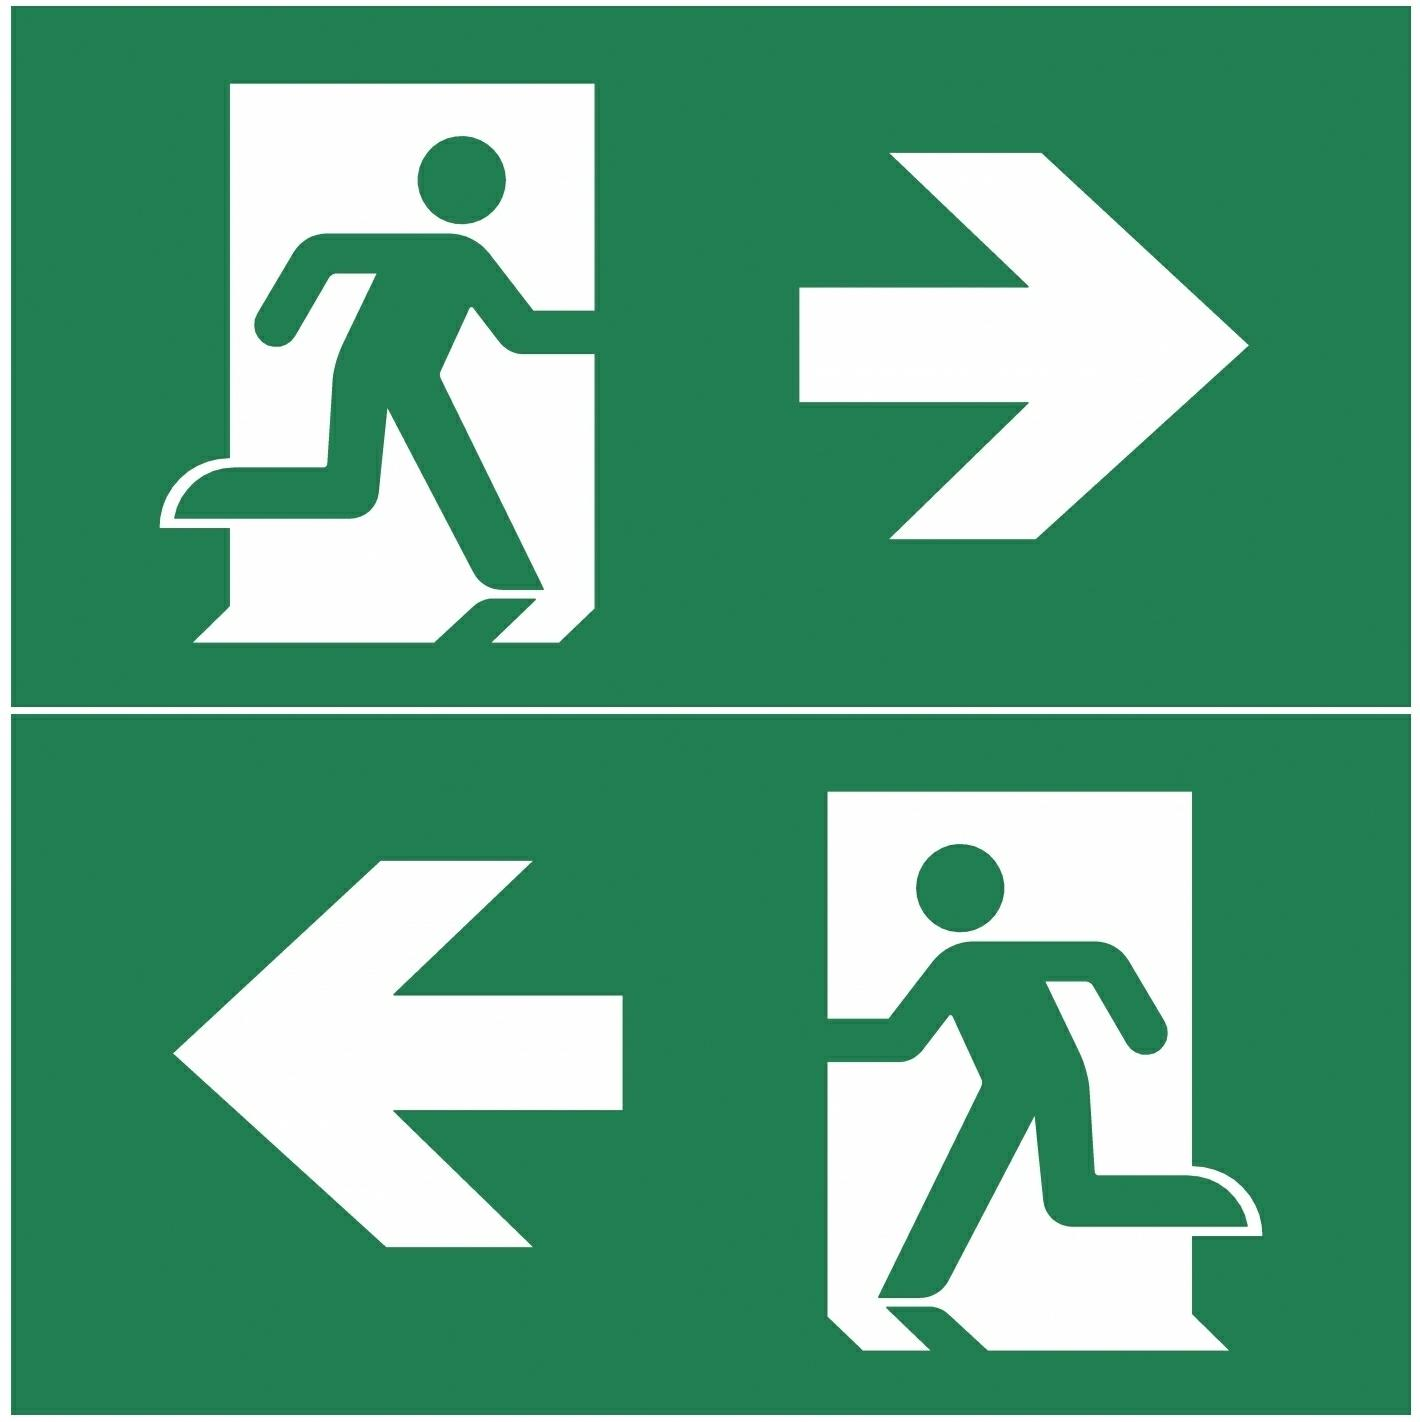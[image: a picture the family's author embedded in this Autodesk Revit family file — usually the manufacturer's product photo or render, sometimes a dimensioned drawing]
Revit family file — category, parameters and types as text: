
# Revit family: TWS8092WA
name_source: partatom
category: Lighting Fixtures
revit_build: Autodesk Revit 2016 (Build: 20150714_1515(x64)
units: mm (PartAtom-declared; Revit-internal decimal feet)

## family parameters
Always vertical = Yes
Cut with Voids When Loaded = No
Light Source = No
OmniClass Number = 23.80.70.00
OmniClass Title = Lighting
Part Type = Normal
Room Calculation Point = No
Round Connector Dimension = Use Diameter
Shared = No
Work Plane-Based = No

## types (6) — shared parameters
Aperture for Recess Mounting = 53 mm x 275 mm
Body Material = Plastic
Color = RAL9003
Customs Code = 94056080
Description = Self-Contained LED Exit Light with 1 h Super Capacitor Backup and Wireless Monitoring
ETIM Product Class = EC001957
Electrical Installation = 2/3 x 2,5 mm² -o-
Feature = ESCAP, Aalto Control
GTIN Code = 6438045011868
Glow Wire Test of Plastic Materials = 650 °C
Height = 185 mm  [stored 0.606955 ft]
IP Class = IP44
Keynote = 23
Length = 268 mm  [stored 0.879265 ft]
Light Source = LED
Manufacturer = Teknoware Oy
Max Input Power VA = 4 VA
Model = ESC 80
Mounting_Optional = Recess, Flag, Pendel
Mounting_Standard = Wall, Ceiling
Nominal Supply Voltage = 220-240 V, 50/60 Hz AC
Product Code = TWS8092WA
Protection Class = II
Sähkönumerot.fi -tuotesivu = http://www.sahkonumerot.fi
Type Image = ESC80.jpg
URL = http://www.teknoware.com
Viewing Distance = 20000 mm  [stored 65.6168 ft]
Wattage Comments = LED
Weight = 0.80 kg
Width = 40 mm  [stored 0.131234 ft]

## per-type parameters (varying)
| type | Max Input Power W | Pictogram Type | Sähkönumero | Temperature Range Min_Max |
| Arrow down 20m | 0 W | OPASTE PBV80202E | 4211321 | -25...+35 °C |
| Arrow down 30m | 0 W | OPASTE PBV80302E | 4211321 | -5...+30 °C |
| Arrow down 26m | 0 W | OPASTE PBV80262E | 4211321 | -5...+30 °C |
| Arrow left_right 20m | 0 W | OPASTE PBV80201E | 4211321 | -5...+30 °C |
| Arrow left_right 26m | 4 W | OPASTE PBV80261E | 4211323 | -5...+30 °C |
| Arrow left_right 30m | 0 W | OPASTE PBV80202E | 4211321 | -25...+35 °C |

note: [stored X ft] marks values corroborated as IEEE doubles in the binary element streams (Revit-internal decimal feet)

## geometry (parser evidence)
native form markers: Sweep x24
no freeform markers — native parametric forms only
